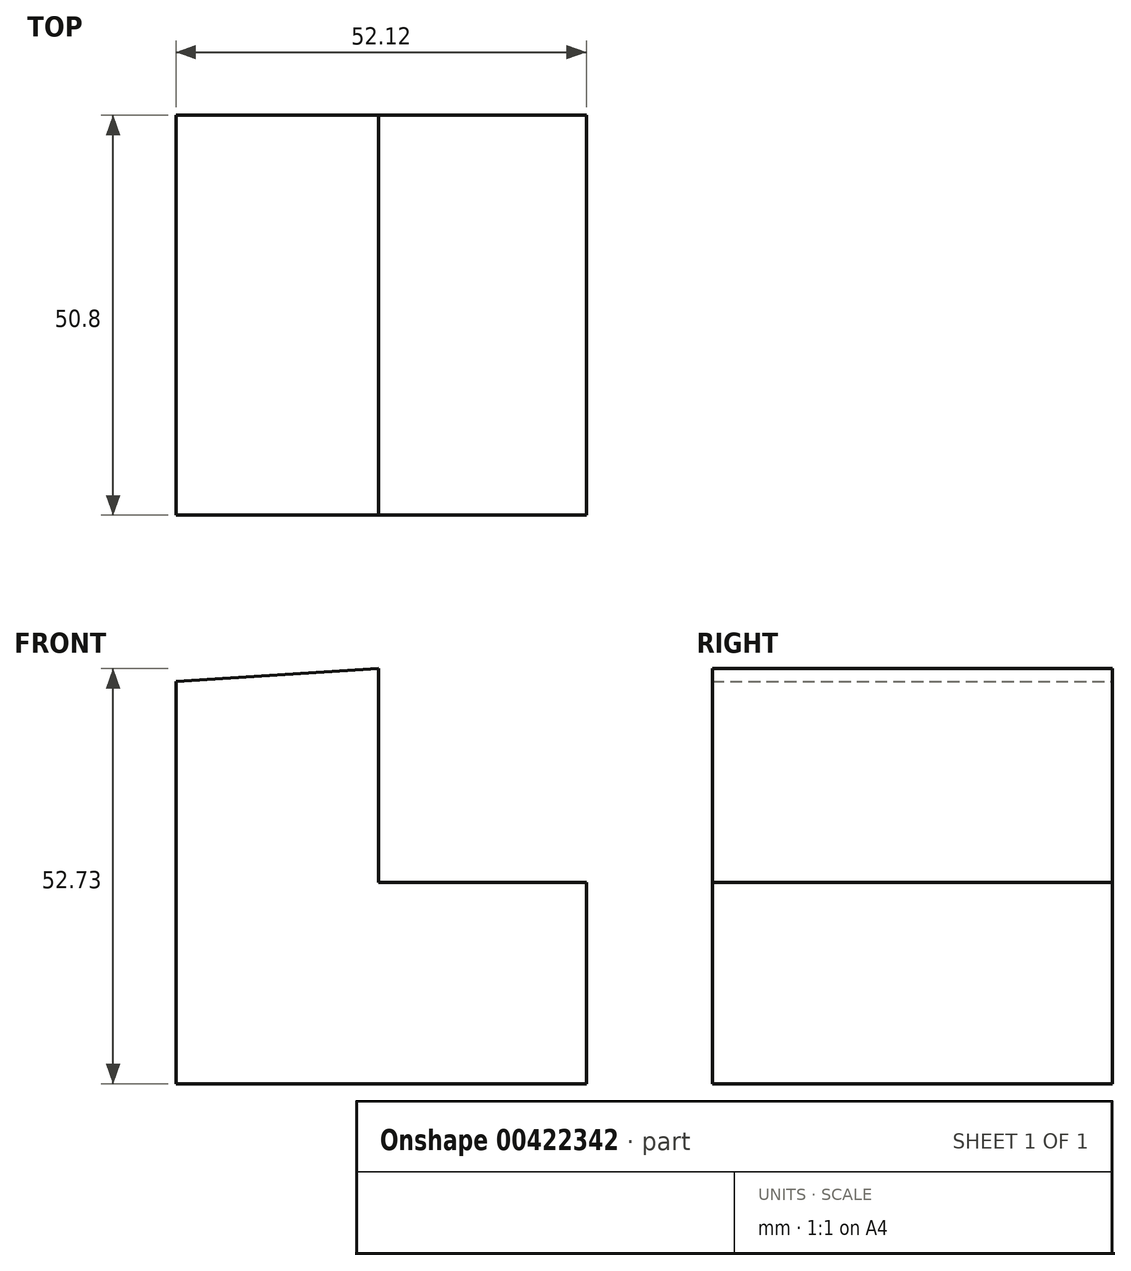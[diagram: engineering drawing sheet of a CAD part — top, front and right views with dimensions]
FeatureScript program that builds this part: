
annotation { "Feature Type Name" : "Feature", "Feature Type Description" : "" }
export const myFeature = defineFeature(function(context is Context, id is Id, definition is map)
    precondition{}
    {
        {
            var Q0;
            Q0=qCreatedBy(makeId("Front.planeOp"),FACE);
            var sketch = newSketch(context, id + "F0", { "sketchPlane" : qUnion([Q0])});
            skLineSegment(sketch, "E0", {"start": v(-39.85, 38.03) * mm, "end": v(-39.85, -13.08) * mm});
            skLineSegment(sketch, "E1", {"start": v(-39.85, -13.08) * mm, "end": v(12.27, -13.08) * mm});
            skLineSegment(sketch, "E2", {"start": v(12.27, -13.08) * mm, "end": v(12.27, 12.47) * mm});
            skLineSegment(sketch, "E3", {"start": v(12.27, 12.47) * mm, "end": v(-14.1, 12.47) * mm});
            skLineSegment(sketch, "E4", {"start": v(-14.1, 12.47) * mm, "end": v(-14.1, 39.65) * mm});
            skLineSegment(sketch, "E5", {"start": v(-14.1, 39.65) * mm, "end": v(-39.85, 38.03) * mm});
            skSolve(sketch);
        }
        {
            var Q0;
            Q0 = qSketchRegion(id + "F0", true);
            extrude(context, id + "F1", {"entities" : qUnion([Q0]), "depth" : 50.8 * mm});
        }
    });
